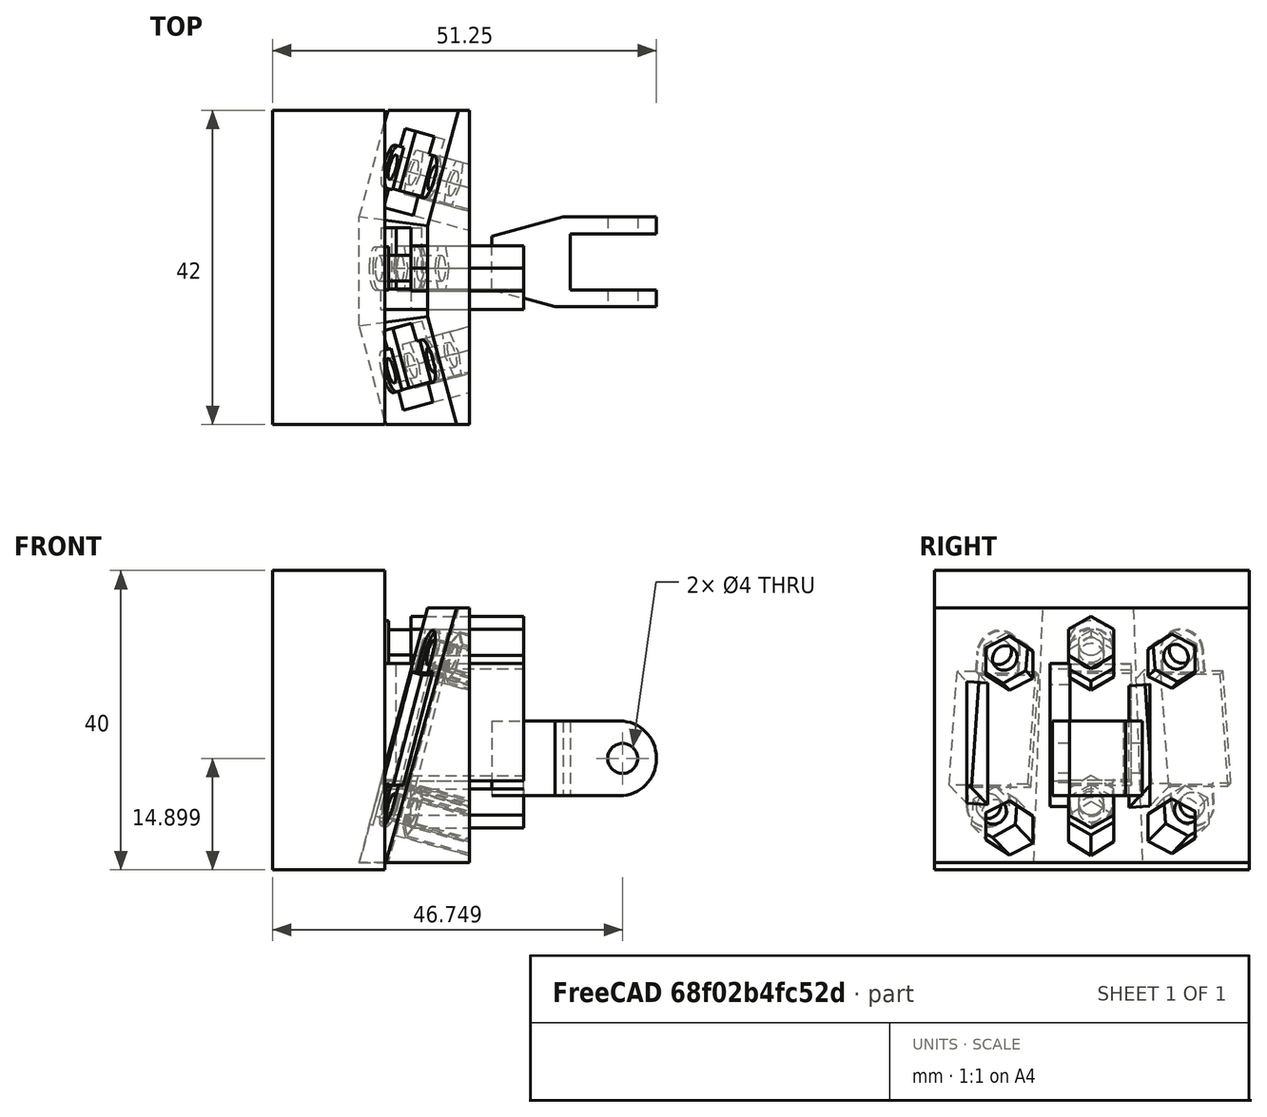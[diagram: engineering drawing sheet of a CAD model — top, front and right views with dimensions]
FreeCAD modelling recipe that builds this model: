
FCSTD DOCUMENT  (FreeCAD 0.18R4 (GitTag))
Label: ToF Sensor
License: All rights reserved
LicenseURL: http://en.wikipedia.org/wiki/All_rights_reserved
objects: Part::MultiFuse×12, Part::Box×9, Part::Cylinder×7, Part::Cut×7, Part::Prism×2, Part::Compound×1, Part::Fillet×1
note: 39 computed .brp shape members not serialized (recipe doc carries the construction recipe); baked Part::Feature solids carry a one-line shape summary decoded from their .brp

FEATURE [Part::Cylinder] Cylinder259  label="Zylinder261"
  Angle = 360
  AttacherType = Attacher::AttachEngine3D
  Height = 20
  Placement = pos=(-6e-15,5.4,18.4) rot=(0,1,0;1.5708rad)
  Radius = 1.7
FEATURE [Part::Cylinder] Cylinder258  label="Zylinder260"
  Angle = 360
  AttacherType = Attacher::AttachEngine3D
  Height = 20
  Placement = pos=(-1e-15,5.4,-2.9) rot=(0,1,0;1.5708rad)
  Radius = 1.7
FEATURE [Part::Compound] Compound
  Links = -> [Cylinder258,Cylinder259]
FEATURE [Part::Cylinder] Cylinder256  label="Zylinder258"
  Angle = 360
  AttacherType = Attacher::AttachEngine3D
  Height = 2
  Placement = pos=(-1e-15,5.4,-2.9) rot=(0,1,0;1.5708rad)
  Radius = 2.9
FEATURE [Part::Box] Box180  label="Würfel169"
  AttacherType = Attacher::AttachEngine3D
  Height = 15.5
  Length = 3
  Width = 10.8
FEATURE [Part::Cylinder] Cylinder257  label="Zylinder259"
  Angle = 360
  AttacherType = Attacher::AttachEngine3D
  Height = 2
  Placement = pos=(-6e-15,5.4,18.4) rot=(0,1,0;1.5708rad)
  Radius = 2.9
FEATURE [Part::Box] Box181  label="Würfel170"
  AttacherType = Attacher::AttachEngine3D
  Height = 21.3
  Length = 2
  Placement = pos=(0,2.5,-2.9) rot=(0,0,1;0rad)
  Width = 5.8
FEATURE [Part::MultiFuse] Fusion176
  Shapes = -> [Cylinder257,Cylinder256,Box181]
FEATURE [Part::Cut] Cut119
  Base = -> Fusion176
  Tool = -> Compound
FEATURE [Part::MultiFuse] Fusion177  label="ToF Halter"
  Shapes = -> [Box180,Cut119]
FEATURE [Part::Box] Box  label="Würfel"
  AttacherType = Attacher::AttachEngine3D
  Height = 15.7
  Length = 20
  Placement = pos=(0,-0.1,-0.1) rot=(0,0,1;0rad)
  Width = 2.7
FEATURE [Part::Prism] Prism  label="Prisma"
  AttacherType = Attacher::AttachEngine3D
  Circumradius = 3.5
  Height = 15
  Placement = pos=(5,5.4,-2.9) rot=(0,1,0;1.5708rad)
  Polygon = 6
FEATURE [Part::Prism] Prism001  label="Prisma001"
  AttacherType = Attacher::AttachEngine3D
  Circumradius = 3.5
  Height = 15
  Placement = pos=(5,5.4,18.4) rot=(0,1,0;1.5708rad)
  Polygon = 6
FEATURE [Part::Cylinder] Cylinder260  label="Zylinder262"
  Angle = 360
  AttacherType = Attacher::AttachEngine3D
  Height = 20
  Placement = pos=(-1e-15,5.4,-2.9) rot=(0,1,0;1.5708rad)
  Radius = 1.7
FEATURE [Part::Cylinder] Cylinder261  label="Zylinder263"
  Angle = 360
  AttacherType = Attacher::AttachEngine3D
  Height = 20
  Placement = pos=(-6e-15,5.4,18.4) rot=(0,1,0;1.5708rad)
  Radius = 1.7
FEATURE [Part::Box] Box182  label="Würfel171"
  AttacherType = Attacher::AttachEngine3D
  Height = 40
  Length = 15
  Placement = pos=(-13.5,-15.5,-12) rot=(0,0,1;0rad)
  Width = 42
FEATURE [Part::Box] Box195  label="Halterblock"
  AttacherType = Attacher::AttachEngine3D
  Height = 34
  Length = 15
  Placement = pos=(-2.2,-15.5,-11) rot=(0,0,1;0rad)
  Width = 42
FEATURE [Part::MultiFuse] Fusion
  Shapes = -> [Cylinder260,Prism]
FEATURE [Part::MultiFuse] Fusion178
  Shapes = -> [Cylinder261,Prism001]
FEATURE [Part::MultiFuse] Fusion179
  Shapes = -> [Fusion177,Box]
FEATURE [Part::MultiFuse] Fusion180
  Shapes = -> [Fusion179,Fusion178]
FEATURE [Part::MultiFuse] Fusion181
  Shapes = -> [Fusion,Fusion180]
FEATURE [Part::MultiFuse] Fusion182  label="Sensorstempel"
  Shapes = -> [Box182,Fusion181]
FEATURE [Part::MultiFuse] Fusion186  label="Stempel Mitte"
  Placement = pos=(-0.482963,0,0.12941) rot=(0,1,0;0.261799rad)
  Shapes = -> [Box182,Fusion181]
FEATURE [Part::MultiFuse] Fusion194  label="Stempel Links"
  Placement = pos=(2.58694,-13.8245,-0.164085) rot=(-0.092692,0.704063,0.704063;0.36971rad)
  Shapes = -> [Box182,Fusion181]
FEATURE [Part::MultiFuse] Fusion202  label="Stempel Rechts"
  Placement = pos=(0,14,0) rot=(0.092692,0.704063,-0.704063;0.36971rad)
  Shapes = -> [Box182,Fusion181]
FEATURE [Part::Cut] Cut
  Base = -> Box195
  Tool = -> Fusion186
FEATURE [Part::Cut] Cut123
  Base = -> Cut
  Tool = -> Fusion202
FEATURE [Part::Cut] Cut124  label="Sensorhalter"
  Base = -> Cut123
  Tool = -> Fusion194
FEATURE [Part::Cylinder] Cylinder240  label="Zylinder242"
  Angle = 360
  AttacherType = Attacher::AttachEngine3D
  Height = 15
  Placement = pos=(37.5,7.5,-5.5) rot=(1,0,0;1.5708rad)
  Radius = 2
FEATURE [Part::Box] Box162  label="Würfel151"
  AttacherType = Attacher::AttachEngine3D
  Height = 12
  Length = 16
  Placement = pos=(28.5,-3.75,-11.5) rot=(0,0,1;0rad)
  Width = 7.5
FEATURE [Part::Box] Box163  label="Würfel152"
  AttacherType = Attacher::AttachEngine3D
  Height = 10
  Length = 22
  Placement = pos=(27,-3.5,-10.5) rot=(0,0,1;0rad)
  Width = 12
FEATURE [Part::Fillet] Fillet099
  Base = -> Box163
  Edges = 2 edges r=4.9: [Edge6,Edge8]
  Placement = pos=(82,-2.5,-11) rot=(0,1,0;3.14159rad)
FEATURE [Part::Box] Box188  label="Würfel184"
  AttacherType = Attacher::AttachEngine3D
  Height = 15
  Length = 2.7
  Placement = pos=(16.4898,0.0776457,7.9) rot=(0,0,1;0.261799rad)
  Width = 15
FEATURE [Part::MultiFuse] Fusion160
  Shapes = -> [Cylinder240,Box162]
FEATURE [Part::Cut] Cut110
  Base = -> Fillet099
  Placement = pos=(22.1416,57.2495,8.39933) rot=(0.707107,-0.707107,0;3.14159rad)
  Tool = -> Fusion160
FEATURE [Part::Box] Box208  label="Würfel185"
  AttacherType = Attacher::AttachEngine3D
  Height = 15
  Length = 2.5
  Placement = pos=(24.7001,-2.12232,7.9) rot=(0,0,-1;0.261799rad)
  Width = 15
FEATURE [Part::Cut] Cut127
  Base = -> Cut110
  Tool = -> Box188
FEATURE [Part::Cut] Cut128  label="Verbinder"
  Base = -> Cut127
  Placement = pos=(13.5,28.4,-11) rot=(0,0,-1;1.5708rad)
  Tool = -> Box208
